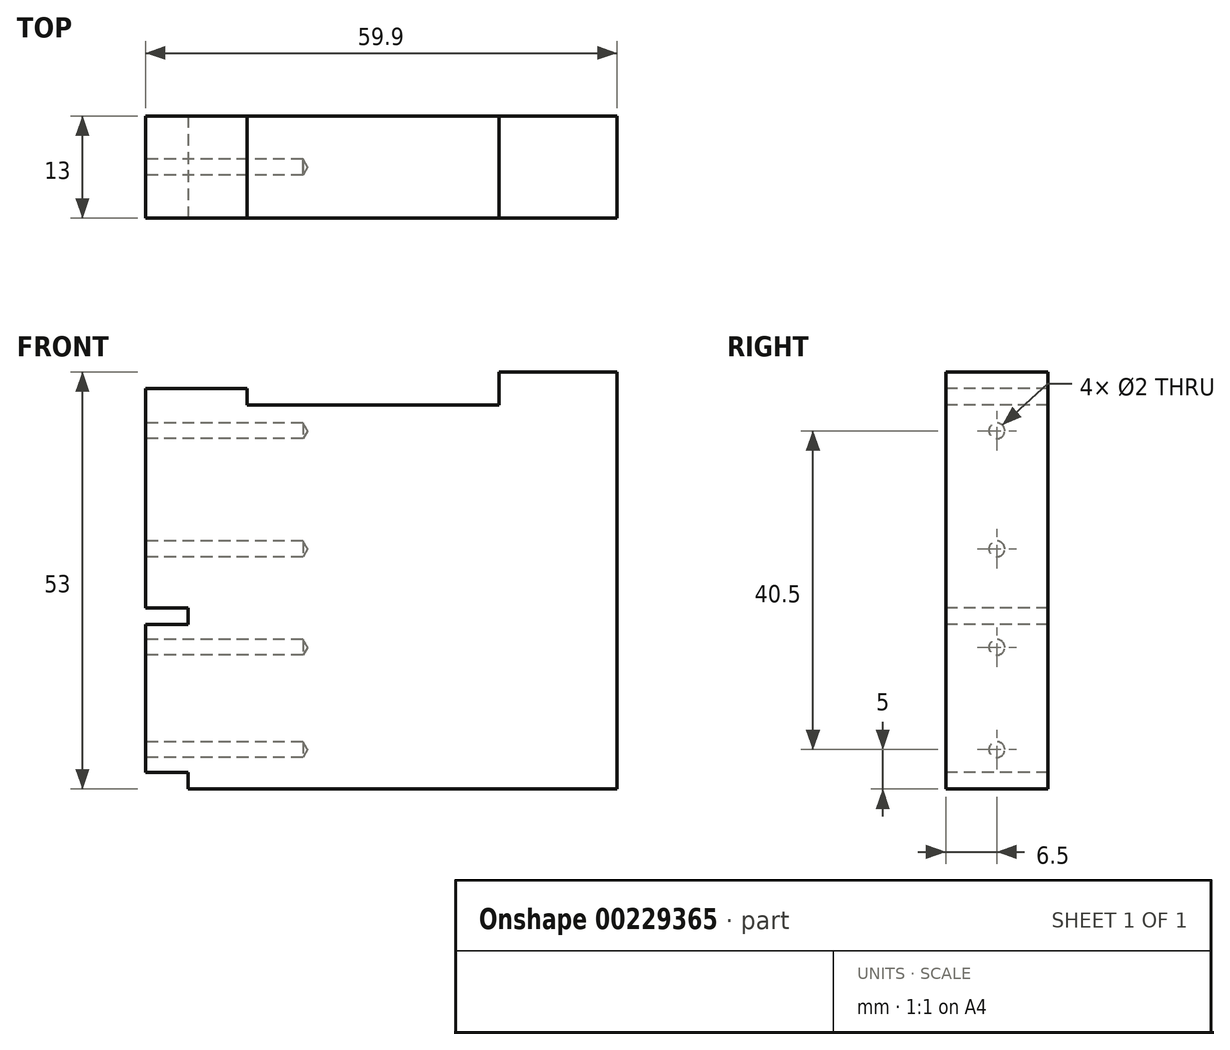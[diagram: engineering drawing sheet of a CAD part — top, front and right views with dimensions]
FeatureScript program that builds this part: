
annotation { "Feature Type Name" : "Feature", "Feature Type Description" : "" }
export const myFeature = defineFeature(function(context is Context, id is Id, definition is map)
    precondition{}
    {
        {
            var Q0;
            Q0=qCreatedBy(makeId("Front.planeOp"),FACE);
            var sketch = newSketch(context, id + "F0", { "sketchPlane" : qUnion([Q0])});
            skLineSegment(sketch, "E0.bottom", {"start": v(31, 26.5) * mm, "end": v(-31, 26.5) * mm});
            skLineSegment(sketch, "E0.top", {"start": v(31, -26.5) * mm, "end": v(-31, -26.5) * mm});
            skLineSegment(sketch, "E0.left", {"start": v(31, 26.5) * mm, "end": v(31, -26.5) * mm});
            skLineSegment(sketch, "E0.right", {"start": v(-31, 26.5) * mm, "end": v(-31, -26.5) * mm});
            skPoint(sketch, "E0.middle", {"position": v(0, 0) * mm});
            skSolve(sketch);
        }
        {
            var Q0;
            Q0=makeQuery(id+"F0.imprint","IMPRINT",FACE,{"disambiguationData":[TD([[makeQuery(id+"F0.imprint","IMPRINT",EDGE,{"derivedFrom":sQuery(id+"F0.wireOp",EDGE,"E0.bottom")}),1.0]])]});
            extrude(context, id + "F1", {"entities" : qUnion([Q0]), "endBound" : BoundingType.SYMMETRIC, "depth" : 13 * mm});
        }
        {
            var Q0;
            Q0=makeQuery(id+"F1.opExtrude","CAP_FACE",FACE,{"disambiguationData":[OSD([sQuery(id+"F0.wireOp",EDGE,"E0.bottom"),sQuery(id+"F0.wireOp",EDGE,"E0.top"),sQuery(id+"F0.wireOp",EDGE,"E0.left"),sQuery(id+"F0.wireOp",EDGE,"E0.right")])],"isStart":false});
            var sketch = newSketch(context, id + "F2", { "sketchPlane" : qUnion([Q0])});
            skLineSegment(sketch, "E1", {"start": v(-31, 26.5) * mm, "end": v(-31, -3.5) * mm});
            skLineSegment(sketch, "E2", {"start": v(-31, -3.5) * mm, "end": v(-28.9, -3.5) * mm});
            skLineSegment(sketch, "E3", {"start": v(-28.9, -3.5) * mm, "end": v(-28.9, 24.4) * mm});
            skLineSegment(sketch, "E4", {"start": v(-28.9, 24.4) * mm, "end": v(-16, 24.4) * mm});
            skLineSegment(sketch, "E5", {"start": v(-16, 24.4) * mm, "end": v(-16, 26.5) * mm});
            skLineSegment(sketch, "E6", {"start": v(-16, 26.5) * mm, "end": v(-31, 26.5) * mm});
            skLineSegment(sketch, "E7", {"start": v(-23.5, -26.5) * mm, "end": v(-31, -26.5) * mm});
            skLineSegment(sketch, "E8", {"start": v(-31, -26.5) * mm, "end": v(-31, -3.5) * mm});
            skLineSegment(sketch, "E9", {"start": v(-31, -3.5) * mm, "end": v(-23.5, -3.5) * mm});
            skLineSegment(sketch, "E10", {"start": v(-23.5, -3.5) * mm, "end": v(-23.5, -5.6) * mm});
            skLineSegment(sketch, "E11", {"start": v(-23.5, -5.6) * mm, "end": v(-28.9, -5.6) * mm});
            skLineSegment(sketch, "E12", {"start": v(-28.9, -5.6) * mm, "end": v(-28.9, -24.4) * mm});
            skLineSegment(sketch, "E13", {"start": v(-28.9, -24.4) * mm, "end": v(-23.5, -24.4) * mm});
            skLineSegment(sketch, "E14", {"start": v(-23.5, -24.4) * mm, "end": v(-23.5, -26.5) * mm});
            skSolve(sketch);
        }
        {
            var Q0;
            {var subQ1=sQuery(id+"F2.wireOp",EDGE,"E1");Q0=makeQuery(id+"F2.imprint","IMPRINT",FACE,{"disambiguationData":[TD([[makeQuery(id+"F2.imprint","IMPRINT",EDGE,{"derivedFrom":subQ1}),1.0]])]});}
            var Q1;
            Q1=makeQuery(id+"F2.imprint","IMPRINT",FACE,{"disambiguationData":[TD([[makeQuery(id+"F2.imprint","IMPRINT",EDGE,{"derivedFrom":sQuery(id+"F2.wireOp",EDGE,"E7")}),-1.0]])]});
            extrude(context, id + "F3", {"entities" : qUnion([Q0, Q1]), "operationType" : NewBodyOperationType.REMOVE, "endBound" : BoundingType.UP_TO_NEXT, "oppositeDirection" : true, "depth" : 25 * mm});
        }
        {
            var Q0;
            Q0=makeQuery(id+"F3.boolean.opBoolean","COPY",FACE,{"derivedFrom":makeQuery(id+"F3.opExtrude","SWEPT_FACE",FACE,{"disambiguationData":[OSD([sQuery(id+"F2.wireOp",EDGE,"E3")])]})});
            var sketch = newSketch(context, id + "F4", { "sketchPlane" : qUnion([Q0])});
            skPoint(sketch, "E15", {"position": v(0, 19) * mm});
            skPoint(sketch, "E16", {"position": v(0, -8.5) * mm});
            skPoint(sketch, "E17", {"position": v(0, -21.5) * mm});
            skPoint(sketch, "E18", {"position": v(0, 4) * mm});
            skSolve(sketch);
        }
        {
            var Q0;
            Q0=sQuery(id+"F4.wireOp",VERTEX,"E15");
            var Q1;
            Q1=sQuery(id+"F4.wireOp",VERTEX,"E18");
            var Q2;
            Q2=sQuery(id+"F4.wireOp",VERTEX,"E16");
            var Q3;
            Q3=sQuery(id+"F4.wireOp",VERTEX,"E17");
            var Q4;
            Q4=makeQuery(id+"F1.opExtrude","SWEPT_BODY",BODY,{"disambiguationData":[OSD([sQuery(id+"F0.wireOp",EDGE,"E0.bottom"),sQuery(id+"F0.wireOp",EDGE,"E0.top"),sQuery(id+"F0.wireOp",EDGE,"E0.left"),sQuery(id+"F0.wireOp",EDGE,"E0.right")])]});
            hole(context, id + "F5", {"style" : HoleStyle.SIMPLE, "endStyle" : HoleEndStyle.BLIND, "holeDiameter" : 2 * mm, "holeDepth" : 20 * mm, "locations" : qUnion([Q0, Q1, Q2, Q3]), "scope" : qUnion([Q4])});
        }
        {
            var Q0;
            Q0=makeQuery(id+"F1.opExtrude","CAP_FACE",FACE,{"disambiguationData":[OSD([sQuery(id+"F0.wireOp",EDGE,"E0.bottom"),sQuery(id+"F0.wireOp",EDGE,"E0.top"),sQuery(id+"F0.wireOp",EDGE,"E0.left"),sQuery(id+"F0.wireOp",EDGE,"E0.right")])],"isStart":false});
            var sketch = newSketch(context, id + "F6", { "sketchPlane" : qUnion([Q0])});
            skLineSegment(sketch, "E19.bottom", {"start": v(-7, 26.5) * mm, "end": v(2, 26.5) * mm});
            skLineSegment(sketch, "E19.top", {"start": v(-7, 22.25) * mm, "end": v(2, 22.25) * mm});
            skLineSegment(sketch, "E19.left", {"start": v(-7, 26.5) * mm, "end": v(-7, 22.25) * mm});
            skLineSegment(sketch, "E19.right", {"start": v(2, 26.5) * mm, "end": v(2, 22.25) * mm});
            skLineSegment(sketch, "E20.bottom", {"start": v(-7, 22.25) * mm, "end": v(-16, 22.25) * mm});
            skLineSegment(sketch, "E20.top", {"start": v(-7, 26.5) * mm, "end": v(-16, 26.5) * mm});
            skLineSegment(sketch, "E20.left", {"start": v(-7, 22.25) * mm, "end": v(-7, 26.5) * mm});
            skLineSegment(sketch, "E20.right", {"start": v(-16, 22.25) * mm, "end": v(-16, 26.5) * mm});
            skLineSegment(sketch, "E21.bottom", {"start": v(2, 22.25) * mm, "end": v(11, 22.25) * mm});
            skLineSegment(sketch, "E21.top", {"start": v(2, 26.5) * mm, "end": v(11, 26.5) * mm});
            skLineSegment(sketch, "E21.left", {"start": v(2, 22.25) * mm, "end": v(2, 26.5) * mm});
            skLineSegment(sketch, "E21.right", {"start": v(11, 22.25) * mm, "end": v(11, 26.5) * mm});
            skLineSegment(sketch, "E22.bottom", {"start": v(11, 22.25) * mm, "end": v(16, 22.25) * mm});
            skLineSegment(sketch, "E22.top", {"start": v(11, 26.5) * mm, "end": v(16, 26.5) * mm});
            skLineSegment(sketch, "E22.right", {"start": v(16, 22.25) * mm, "end": v(16, 26.5) * mm});
            skSolve(sketch);
        }
        {
            var Q0;
            Q0=makeQuery(id+"F6.imprint","IMPRINT",FACE,{"disambiguationData":[TD([[makeQuery(id+"F6.imprint","IMPRINT",EDGE,{"derivedFrom":sQuery(id+"F6.wireOp",EDGE,"E19.bottom")}),1.0]])]});
            var Q1;
            {var subQ2=sQuery(id+"F6.wireOp",EDGE,"E20.bottom");Q1=makeQuery(id+"F6.imprint","IMPRINT",FACE,{"disambiguationData":[TD([[makeQuery(id+"F6.imprint","IMPRINT",EDGE,{"derivedFrom":subQ2}),-1.0]])]});}
            var Q2;
            Q2=makeQuery(id+"F6.imprint","IMPRINT",FACE,{"disambiguationData":[TD([[makeQuery(id+"F6.imprint","IMPRINT",EDGE,{"derivedFrom":sQuery(id+"F6.wireOp",EDGE,"E21.bottom")}),1.0]])]});
            var Q3;
            {var subQ2=sQuery(id+"F6.wireOp",EDGE,"E22.bottom");Q3=makeQuery(id+"F6.imprint","IMPRINT",FACE,{"disambiguationData":[TD([[makeQuery(id+"F6.imprint","IMPRINT",EDGE,{"derivedFrom":subQ2}),1.0]])]});}
            extrude(context, id + "F7", {"entities" : qUnion([Q0, Q1, Q2, Q3]), "operationType" : NewBodyOperationType.REMOVE, "endBound" : BoundingType.UP_TO_NEXT, "oppositeDirection" : true, "depth" : 25 * mm});
        }
    });
